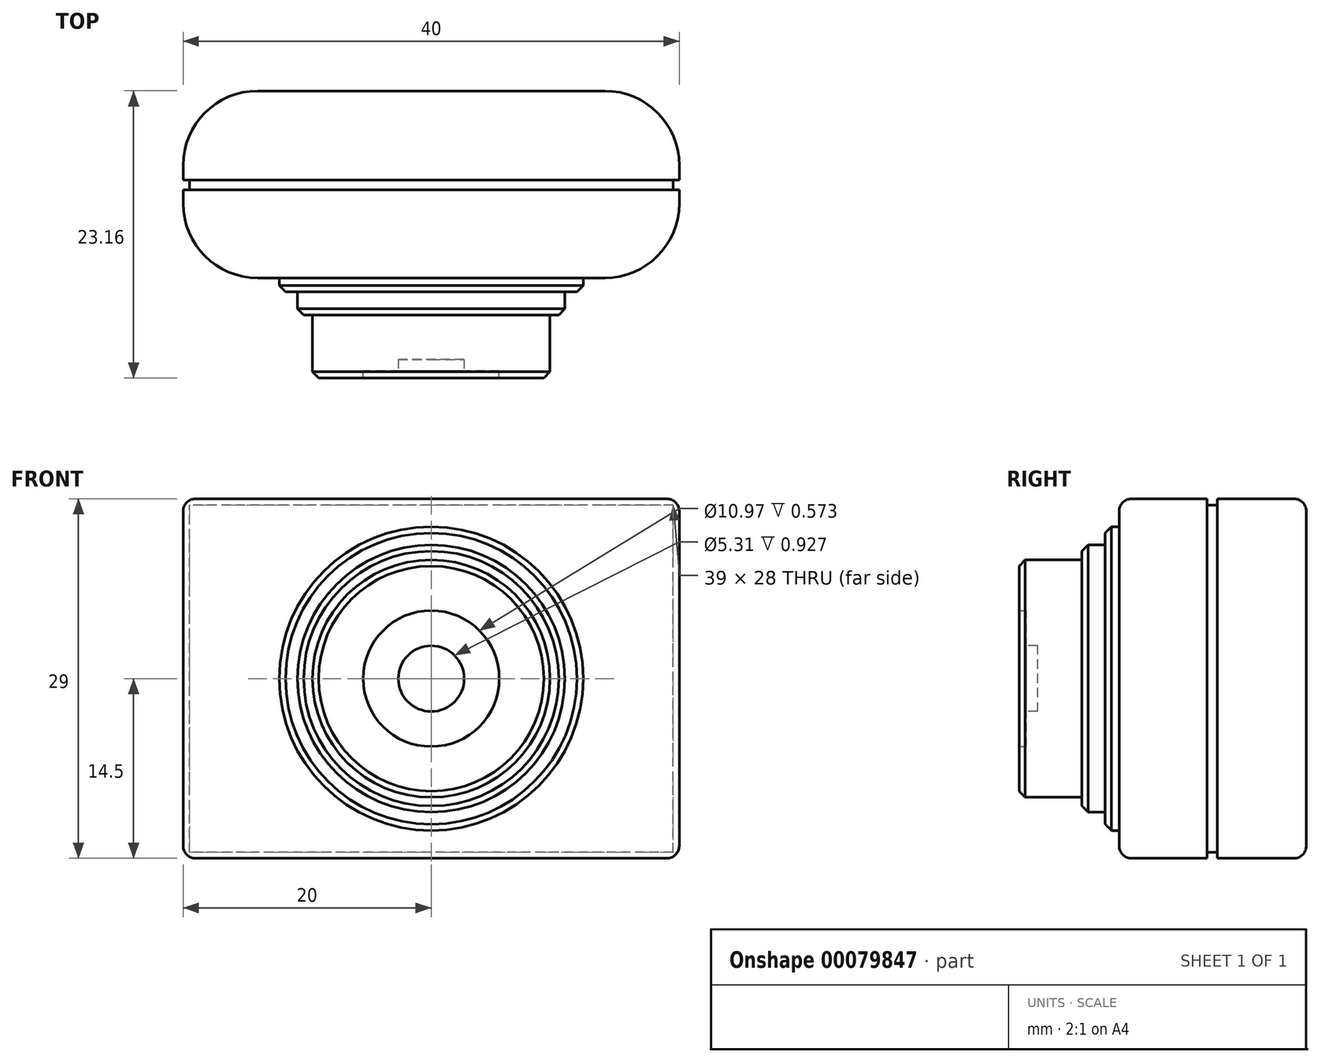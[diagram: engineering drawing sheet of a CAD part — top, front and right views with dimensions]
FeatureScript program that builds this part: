
annotation { "Feature Type Name" : "Feature", "Feature Type Description" : "" }
export const myFeature = defineFeature(function(context is Context, id is Id, definition is map)
    precondition{}
    {
        {
            var Q0;
            Q0=qCreatedBy(makeId("Front.planeOp"),FACE);
            var sketch = newSketch(context, id + "F0", { "sketchPlane" : qUnion([Q0])});
            skCircle(sketch, "E0", {"center": v(0, 0) * mm, "radius": 5.48 * mm});
            skCircle(sketch, "E1", {"center": v(0, 0) * mm, "radius": 9.56 * mm});
            skCircle(sketch, "E2", {"center": v(0, 0) * mm, "radius": 10.83 * mm});
            skCircle(sketch, "E3", {"center": v(0, 0) * mm, "radius": 12.22 * mm});
            skLineSegment(sketch, "E4.bottom", {"start": v(20, -14.5) * mm, "end": v(-20, -14.5) * mm});
            skLineSegment(sketch, "E4.top", {"start": v(20, 14.5) * mm, "end": v(-20, 14.5) * mm});
            skLineSegment(sketch, "E4.left", {"start": v(20, -14.5) * mm, "end": v(20, 14.5) * mm});
            skLineSegment(sketch, "E4.right", {"start": v(-20, -14.5) * mm, "end": v(-20, 14.5) * mm});
            skCircle(sketch, "E5", {"center": v(0, 0) * mm, "radius": 2.65 * mm});
            skSolve(sketch);
        }
        {
            var Q0;
            Q0=qCreatedBy(makeId("Right.planeOp"),FACE);
            var sketch = newSketch(context, id + "F1", { "sketchPlane" : qUnion([Q0])});
            skLineSegment(sketch, "E6.bottom", {"start": v(0, 15.68) * mm, "end": v(15, 15.68) * mm});
            skLineSegment(sketch, "E6.top", {"start": v(0, -15.68) * mm, "end": v(15, -15.68) * mm});
            skLineSegment(sketch, "E6.left", {"start": v(0, 15.68) * mm, "end": v(0, -15.68) * mm});
            skLineSegment(sketch, "E6.right", {"start": v(15, 15.68) * mm, "end": v(15, -15.68) * mm});
            skLineSegment(sketch, "E7.bottom", {"start": v(0, 12.25) * mm, "end": v(-1.13, 12.25) * mm});
            skLineSegment(sketch, "E7.top", {"start": v(0, -12.25) * mm, "end": v(-1.13, -12.25) * mm});
            skLineSegment(sketch, "E7.left", {"start": v(0, 12.25) * mm, "end": v(0, -12.25) * mm});
            skLineSegment(sketch, "E7.right", {"start": v(-1.13, 12.25) * mm, "end": v(-1.13, -12.25) * mm});
            skLineSegment(sketch, "E8.bottom", {"start": v(-1.13, 10.78) * mm, "end": v(-3, 10.78) * mm});
            skLineSegment(sketch, "E8.top", {"start": v(-1.13, -10.78) * mm, "end": v(-3, -10.78) * mm});
            skLineSegment(sketch, "E8.left", {"start": v(-1.13, 10.78) * mm, "end": v(-1.13, -10.78) * mm});
            skLineSegment(sketch, "E8.right", {"start": v(-3, 10.78) * mm, "end": v(-3, -10.78) * mm});
            skLineSegment(sketch, "E9.bottom", {"start": v(-3, 9.58) * mm, "end": v(-8.07, 9.58) * mm});
            skLineSegment(sketch, "E9.top", {"start": v(-3, -9.58) * mm, "end": v(-8.07, -9.58) * mm});
            skLineSegment(sketch, "E9.left", {"start": v(-3, 9.58) * mm, "end": v(-3, -9.58) * mm});
            skLineSegment(sketch, "E9.right", {"start": v(-8.07, 9.58) * mm, "end": v(-8.07, -9.58) * mm});
            skLineSegment(sketch, "E10", {"start": v(0, 0) * mm, "end": v(-8.07, 0) * mm});
            skPoint(sketch, "E10.endSnap0", {"position": v(-1.13, 0) * mm});
            skSolve(sketch);
        }
        {
            var Q0;
            Q0=makeQuery(id+"F0.imprint","IMPRINT",FACE,{"disambiguationData":[TD([[makeQuery(id+"F0.imprint","IMPRINT",EDGE,{"derivedFrom":sQuery(id+"F0.wireOp",EDGE,"E3")}),-1.0]])]});
            var Q1;
            Q1=makeQuery(id+"F0.imprint","IMPRINT",FACE,{"disambiguationData":[TD([[makeQuery(id+"F0.imprint","IMPRINT",EDGE,{"derivedFrom":sQuery(id+"F0.wireOp",EDGE,"E1")}),-1.0]])]});
            var Q2;
            Q2=makeQuery(id+"F0.imprint","IMPRINT",FACE,{"disambiguationData":[TD([[makeQuery(id+"F0.imprint","IMPRINT",EDGE,{"derivedFrom":sQuery(id+"F0.wireOp",EDGE,"E2")}),-1.0]])]});
            var Q3;
            Q3=makeQuery(id+"F0.imprint","IMPRINT",FACE,{"disambiguationData":[TD([[makeQuery(id+"F0.imprint","IMPRINT",EDGE,{"derivedFrom":sQuery(id+"F0.wireOp",EDGE,"E0")}),-1.0]])]});
            var Q4;
            Q4=makeQuery(id+"F0.imprint","IMPRINT",FACE,{"disambiguationData":[TD([[makeQuery(id+"F0.imprint","IMPRINT",EDGE,{"derivedFrom":sQuery(id+"F0.wireOp",EDGE,"E5")}),1.0]])]});
            var Q5;
            Q5=makeQuery(id+"F0.imprint","IMPRINT",FACE,{"disambiguationData":[TD([[makeQuery(id+"F0.imprint","IMPRINT",EDGE,{"derivedFrom":sQuery(id+"F0.wireOp",EDGE,"E0")}),1.0]])]});
            extrude(context, id + "F2", {"entities" : qUnion([Q0, Q1, Q2, Q3, Q4, Q5]), "oppositeDirection" : true, "depth" : 15.1 * mm});
        }
        {
            var Q0;
            {var subQ5=sQuery(id+"F1.wireOp",EDGE,"E7.bottom");Q0=makeQuery(id+"F1.imprint","IMPRINT",FACE,{"disambiguationData":[TD([[makeQuery(id+"F1.imprint","IMPRINT",EDGE,{"derivedFrom":subQ5}),1.0]])]});}
            var Q1;
            {var subQ5=sQuery(id+"F1.wireOp",EDGE,"E8.bottom");Q1=makeQuery(id+"F1.imprint","IMPRINT",FACE,{"disambiguationData":[TD([[makeQuery(id+"F1.imprint","IMPRINT",EDGE,{"derivedFrom":subQ5}),1.0]])]});}
            var Q2;
            {var subQ0=sQuery(id+"F1.wireOp",EDGE,"E9.bottom");Q2=makeQuery(id+"F1.imprint","IMPRINT",FACE,{"disambiguationData":[TD([[makeQuery(id+"F1.imprint","IMPRINT",EDGE,{"derivedFrom":subQ0}),1.0]])]});}
            var Q3;
            Q3=sQuery(id+"F1.wireOp",EDGE,"E10");
            revolve(context, id + "F3", {"entities" : qUnion([Q0, Q1, Q2]), "axis" : qUnion([Q3]), "revolveType" : RevolveType.FULL});
        }
        {
            var Q0;
            Q0=makeQuery(id+"F0.imprint","IMPRINT",FACE,{"disambiguationData":[TD([[makeQuery(id+"F0.imprint","IMPRINT",EDGE,{"derivedFrom":sQuery(id+"F0.wireOp",EDGE,"E0")}),1.0]])]});
            var Q1;
            Q1=makeQuery(id+"F3.opRevolve","SWEPT_FACE",FACE,{"disambiguationData":[OSD([sQuery(id+"F1.wireOp",EDGE,"E9.right")])]});
            extrude(context, id + "F4", {"entities" : qUnion([Q0]), "operationType" : NewBodyOperationType.REMOVE, "endBound" : BoundingType.UP_TO_SURFACE, "endBoundEntityFace" : qUnion([Q1]), "depth" : 25 * mm, "hasSecondDirection" : true, "secondDirectionOppositeDirection" : false, "secondDirectionDepth" : 7.5 * mm});
        }
        {
            var Q0;
            Q0=makeQuery(id+"F4.boolean.opBoolean","SPLIT",FACE,{"disambiguationData":[TD([makeQuery(id+"F4.opExtrude","SWEPT_FACE",FACE,{"disambiguationData":[OSD([sQuery(id+"F0.wireOp",EDGE,"E5")])]})])],"derivedFrom":makeQuery(id+"F3.opRevolve","SWEPT_FACE",FACE,{"disambiguationData":[OSD([sQuery(id+"F1.wireOp",EDGE,"E9.right")])]})});
            extrude(context, id + "F5", {"entities" : qUnion([Q0]), "operationType" : NewBodyOperationType.REMOVE, "oppositeDirection" : true, "depth" : 1.5 * mm});
        }
        {
            var Q0;
            Q0=qCreatedBy(makeId("Front.planeOp"),FACE);
            cPlane(context, id + "F6", {"entities" : qUnion([Q0]), "cplaneType" : CPlaneType.OFFSET, "offset" : 7.5 * mm, "oppositeDirection" : true, "width" : 150 * mm, "height" : 150 * mm});
        }
        {
            var Q0;
            Q0=qCreatedBy(id+"F6.planeOp",FACE);
            var sketch = newSketch(context, id + "F7", { "sketchPlane" : qUnion([Q0])});
            skLineSegment(sketch, "E11.0", {"start": v(20, 14.5) * mm, "end": v(-20, 14.5) * mm});
            skLineSegment(sketch, "E11.1", {"start": v(-20, -14.5) * mm, "end": v(-20, 14.5) * mm});
            skLineSegment(sketch, "E11.2", {"start": v(20, -14.5) * mm, "end": v(20, 14.5) * mm});
            skLineSegment(sketch, "E11.3", {"start": v(20, -14.5) * mm, "end": v(-20, -14.5) * mm});
            skSolve(sketch);
        }
        {
            var Q0;
            Q0=makeQuery(id+"F7.imprint","IMPRINT",FACE,{"disambiguationData":[TD([[makeQuery(id+"F7.imprint","IMPRINT",EDGE,{"derivedFrom":sQuery(id+"F7.wireOp",EDGE,"E11.0")}),1.0]])]});
            extrude(context, id + "F8", {"entities" : qUnion([Q0]), "endBound" : BoundingType.SYMMETRIC, "depth" : 0.8 * mm});
        }
        {
            var Q0;
            Q0=makeQuery(id+"F8.opExtrude","CAP_FACE",FACE,{"disambiguationData":[OSD([sQuery(id+"F7.wireOp",EDGE,"E11.0"),sQuery(id+"F7.wireOp",EDGE,"E11.1"),sQuery(id+"F7.wireOp",EDGE,"E11.2"),sQuery(id+"F7.wireOp",EDGE,"E11.3")])],"isStart":false});
            var Q1;
            Q1=makeQuery(id+"F8.opExtrude","CAP_FACE",FACE,{"disambiguationData":[OSD([sQuery(id+"F7.wireOp",EDGE,"E11.0"),sQuery(id+"F7.wireOp",EDGE,"E11.1"),sQuery(id+"F7.wireOp",EDGE,"E11.2"),sQuery(id+"F7.wireOp",EDGE,"E11.3")])],"isStart":true});
            shell(context, id + "F9", {"entities" : qUnion([Q0, Q1]), "thickness" : 0.5 * mm});
        }
        {
            var Q0;
            Q0=makeQuery(id+"F8.opExtrude","SWEPT_BODY",BODY,{"disambiguationData":[OSD([sQuery(id+"F7.wireOp",EDGE,"E11.0"),sQuery(id+"F7.wireOp",EDGE,"E11.1"),sQuery(id+"F7.wireOp",EDGE,"E11.2"),sQuery(id+"F7.wireOp",EDGE,"E11.3")])]});
            var Q1;
            Q1=makeQuery(id+"F2.opExtrude","SWEPT_BODY",BODY,{"disambiguationData":[OSD([sQuery(id+"F0.wireOp",EDGE,"E4.bottom"),sQuery(id+"F0.wireOp",EDGE,"E4.top"),sQuery(id+"F0.wireOp",EDGE,"E4.left"),sQuery(id+"F0.wireOp",EDGE,"E4.right"),sQuery(id+"F0.wireOp",EDGE,"E5")])]});
            booleanBodies(context, id + "F10", {"operationType" : BooleanOperationType.SUBTRACTION, "tools" : qUnion([Q0]), "targets" : qUnion([Q1])});
        }
        {
            var Q0;
            Q0=makeQuery(id+"F2.opExtrude","CAP_EDGE",EDGE,{"disambiguationData":[OSD([sQuery(id+"F0.wireOp",EDGE,"E4.left")])],"isStart":true});
            var Q1;
            Q1=makeQuery(id+"F2.opExtrude","CAP_EDGE",EDGE,{"disambiguationData":[OSD([sQuery(id+"F0.wireOp",EDGE,"E4.left")])],"isStart":false});
            var Q2;
            Q2=makeQuery(id+"F2.opExtrude","CAP_EDGE",EDGE,{"disambiguationData":[OSD([sQuery(id+"F0.wireOp",EDGE,"E4.right")])],"isStart":true});
            var Q3;
            Q3=makeQuery(id+"F2.opExtrude","CAP_EDGE",EDGE,{"disambiguationData":[OSD([sQuery(id+"F0.wireOp",EDGE,"E4.right")])],"isStart":false});
            fillet(context, id + "F11", {"entities" : qUnion([Q0, Q1, Q2, Q3]), "radius" : 6 * mm, "tangentPropagation" : true, "allowEdgeOverflow" : false});
        }
        {
            var Q0;
            Q0=makeQuery(id+"F2.opExtrude","CAP_EDGE",EDGE,{"disambiguationData":[OSD([sQuery(id+"F0.wireOp",EDGE,"E4.top")])],"isStart":true});
            var Q1;
            Q1=makeQuery(id+"F2.opExtrude","CAP_EDGE",EDGE,{"disambiguationData":[OSD([sQuery(id+"F0.wireOp",EDGE,"E4.top")])],"isStart":false});
            var Q2;
            Q2=makeQuery(id+"F2.opExtrude","CAP_EDGE",EDGE,{"disambiguationData":[OSD([sQuery(id+"F0.wireOp",EDGE,"E4.bottom")])],"isStart":false});
            var Q3;
            Q3=makeQuery(id+"F2.opExtrude","CAP_EDGE",EDGE,{"disambiguationData":[OSD([sQuery(id+"F0.wireOp",EDGE,"E4.bottom")])],"isStart":true});
            fillet(context, id + "F12", {"entities" : qUnion([Q0, Q1, Q2, Q3]), "radius" : 1 * mm, "tangentPropagation" : true, "allowEdgeOverflow" : false});
        }
        {
            var Q0;
            Q0=makeQuery(id+"F3.opRevolve","SWEPT_EDGE",EDGE,{"disambiguationData":[OSD([sQuery(id+"F1.wireOp",EDGE,"E9.bottom"),sQuery(id+"F1.wireOp",EDGE,"E9.right")])]});
            var Q1;
            Q1=makeQuery(id+"F3.opRevolve","SWEPT_EDGE",EDGE,{"disambiguationData":[OSD([sQuery(id+"F1.wireOp",EDGE,"E8.bottom"),sQuery(id+"F1.wireOp",EDGE,"E8.right")])]});
            var Q2;
            Q2=makeQuery(id+"F3.opRevolve","SWEPT_EDGE",EDGE,{"disambiguationData":[OSD([sQuery(id+"F1.wireOp",EDGE,"E7.bottom"),sQuery(id+"F1.wireOp",EDGE,"E7.right")])]});
            var Q3;
            Q3=makeQuery(id+"F4.boolean.opBoolean","COPY",EDGE,{"derivedFrom":makeQuery(id+"F4.opExtrude","CAP_EDGE",EDGE,{"disambiguationData":[OSD([sQuery(id+"F0.wireOp",EDGE,"E0")])],"isStart":false})});
            var Q4;
            Q4=makeQuery(id+"F4.boolean.opBoolean","COPY",EDGE,{"derivedFrom":makeQuery(id+"F4.opExtrude","CAP_EDGE",EDGE,{"disambiguationData":[OSD([sQuery(id+"F0.wireOp",EDGE,"E5")])],"isStart":true})});
            chamfer(context, id + "F13", {"entities" : qUnion([Q0, Q1, Q2, Q3, Q4]), "width" : .5 * mm, "tangentPropagation" : true});
        }
    });
